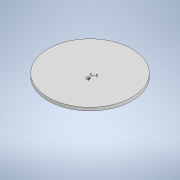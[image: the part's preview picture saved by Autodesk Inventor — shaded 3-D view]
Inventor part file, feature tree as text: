
AUTODESK INVENTOR PART (.ipt)
format: ipt  version: 2020 (Build 240168000, 168)  size: 112,640 bytes
history: native  units: mm
features: extrude x3, sketch x2
ambient origin geometry x8: Origin, YZ Plane, XZ Plane, XY Plane, X Axis, Y Axis, Z Axis, Center Point
bodies: Solid1 (feature_tree)
feature tree (5):
  sketch  "Sketch1"  dims[d0=5.0mm d1=9.0mm]
  extrude  "Extrusion1"  Depth=5.0mm
  extrude  "Extrusion2"  Depth=3.0mm
  extrude  "Extrusion3"  Depth=5.0mm
  sketch  "Sketch2"  dims[d2=25.0mm d3=0.0mm d4=3.0mm d5=80.0mm d6=3.0mm d7=0.0mm d8=5.0mm d9=0.0mm]
